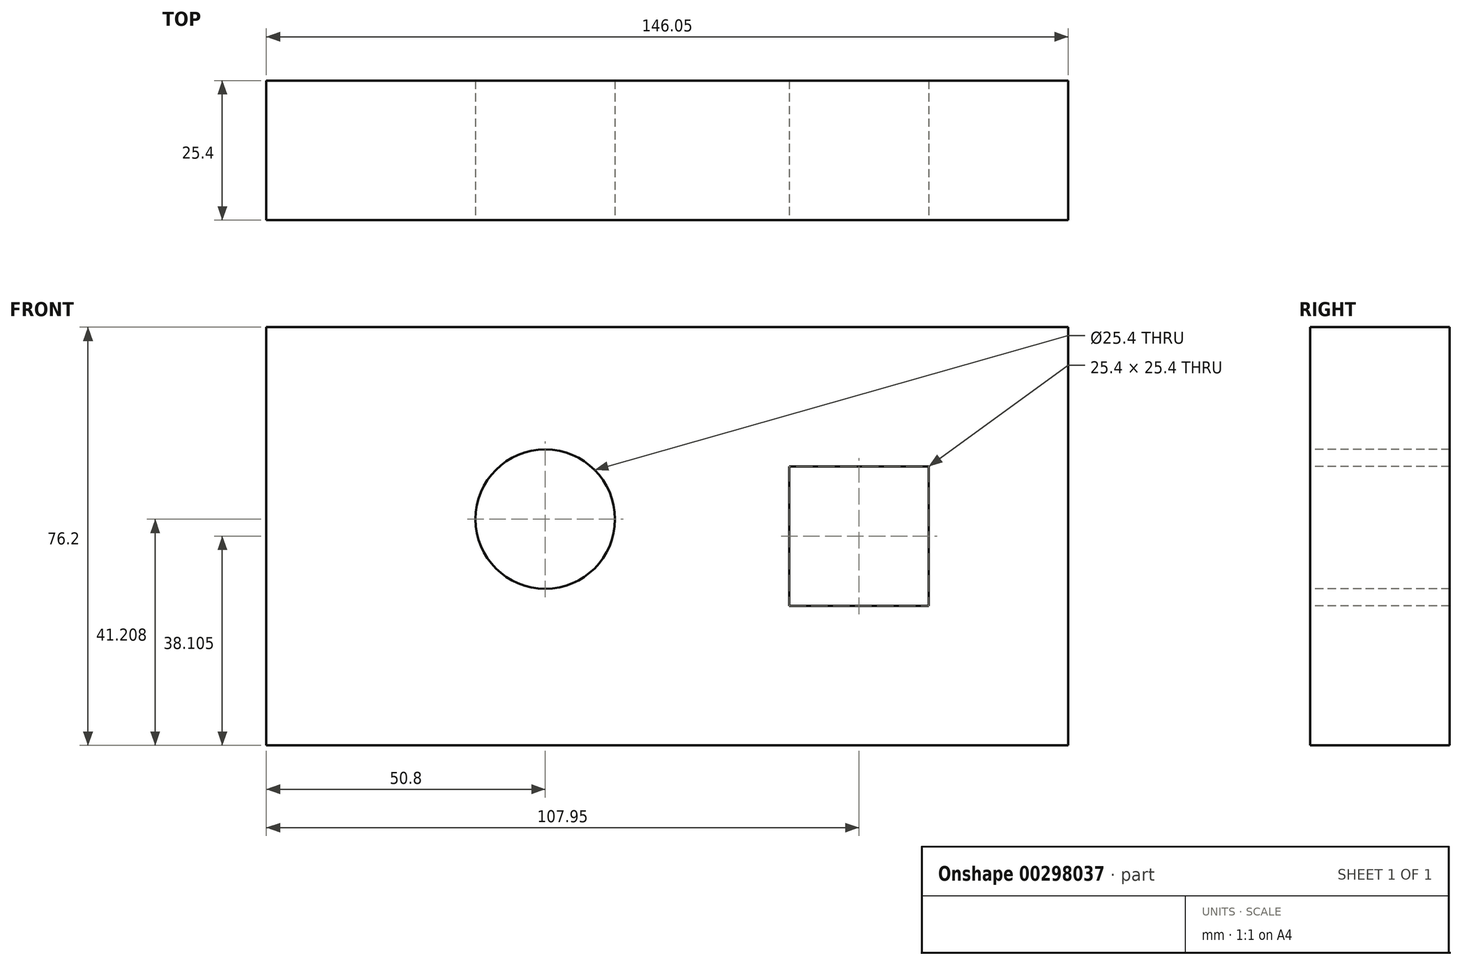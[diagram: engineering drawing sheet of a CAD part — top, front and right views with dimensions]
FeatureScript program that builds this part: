
annotation { "Feature Type Name" : "Feature", "Feature Type Description" : "" }
export const myFeature = defineFeature(function(context is Context, id is Id, definition is map)
    precondition{}
    {
        {
            var Q0;
            Q0=qCreatedBy(makeId("Front.planeOp"),FACE);
            var sketch = newSketch(context, id + "F0", { "sketchPlane" : qUnion([Q0])});
            skLineSegment(sketch, "E0.bottom", {"start": v(-146.05, 95.1) * mm, "end": v(0, 95.1) * mm});
            skLineSegment(sketch, "E0.top", {"start": v(-146.05, 18.9) * mm, "end": v(0, 18.9) * mm});
            skLineSegment(sketch, "E0.left", {"start": v(-146.05, 95.1) * mm, "end": v(-146.05, 18.9) * mm});
            skLineSegment(sketch, "E0.right", {"start": v(0, 95.1) * mm, "end": v(0, 18.9) * mm});
            skSolve(sketch);
        }
        {
            var Q0;
            Q0 = qSketchRegion(id + "F0", true);
            extrude(context, id + "F1", {"entities" : qUnion([Q0]), "depth" : 25.4 * mm});
        }
        {
            var Q0;
            Q0=makeQuery(id+"F1.opExtrude","CAP_FACE",FACE,{"disambiguationData":[OSD([sQuery(id+"F0.wireOp",EDGE,"E0.bottom"),sQuery(id+"F0.wireOp",EDGE,"E0.top"),sQuery(id+"F0.wireOp",EDGE,"E0.left"),sQuery(id+"F0.wireOp",EDGE,"E0.right")])],"isStart":false});
            var sketch = newSketch(context, id + "F2", { "sketchPlane" : qUnion([Q0])});
            skSolve(sketch);
        }
        {
            var Q0;
            Q0=makeQuery(id+"F2.imprint","IMPRINT",FACE,{"disambiguationData":[TD([[makeQuery(id+"F2.imprint","IMPRINT",EDGE,{"derivedFrom":makeQuery(id+"F1.opExtrude","CAP_EDGE",EDGE,{"disambiguationData":[OSD([sQuery(id+"F0.wireOp",EDGE,"E0.bottom")])],"isStart":false})}),-1.0]])]});
            var sketch = newSketch(context, id + "F3", { "sketchPlane" : qUnion([Q0])});
            skCircle(sketch, "E1", {"center": v(-95.25, 60.1) * mm, "radius": 12.7 * mm});
            skLineSegment(sketch, "E2.bottom", {"start": v(-50.8, 69.7) * mm, "end": v(-25.4, 69.7) * mm});
            skLineSegment(sketch, "E2.top", {"start": v(-50.8, 44.3) * mm, "end": v(-25.4, 44.3) * mm});
            skLineSegment(sketch, "E2.left", {"start": v(-50.8, 69.7) * mm, "end": v(-50.8, 44.3) * mm});
            skLineSegment(sketch, "E2.right", {"start": v(-25.4, 69.7) * mm, "end": v(-25.4, 44.3) * mm});
            skSolve(sketch);
        }
        {
            var Q0;
            Q0 = qSketchRegion(id + "F3", true);
            extrude(context, id + "F4", {"entities" : qUnion([Q0]), "operationType" : NewBodyOperationType.REMOVE, "oppositeDirection" : true, "depth" : 25.4 * mm});
        }
    });
